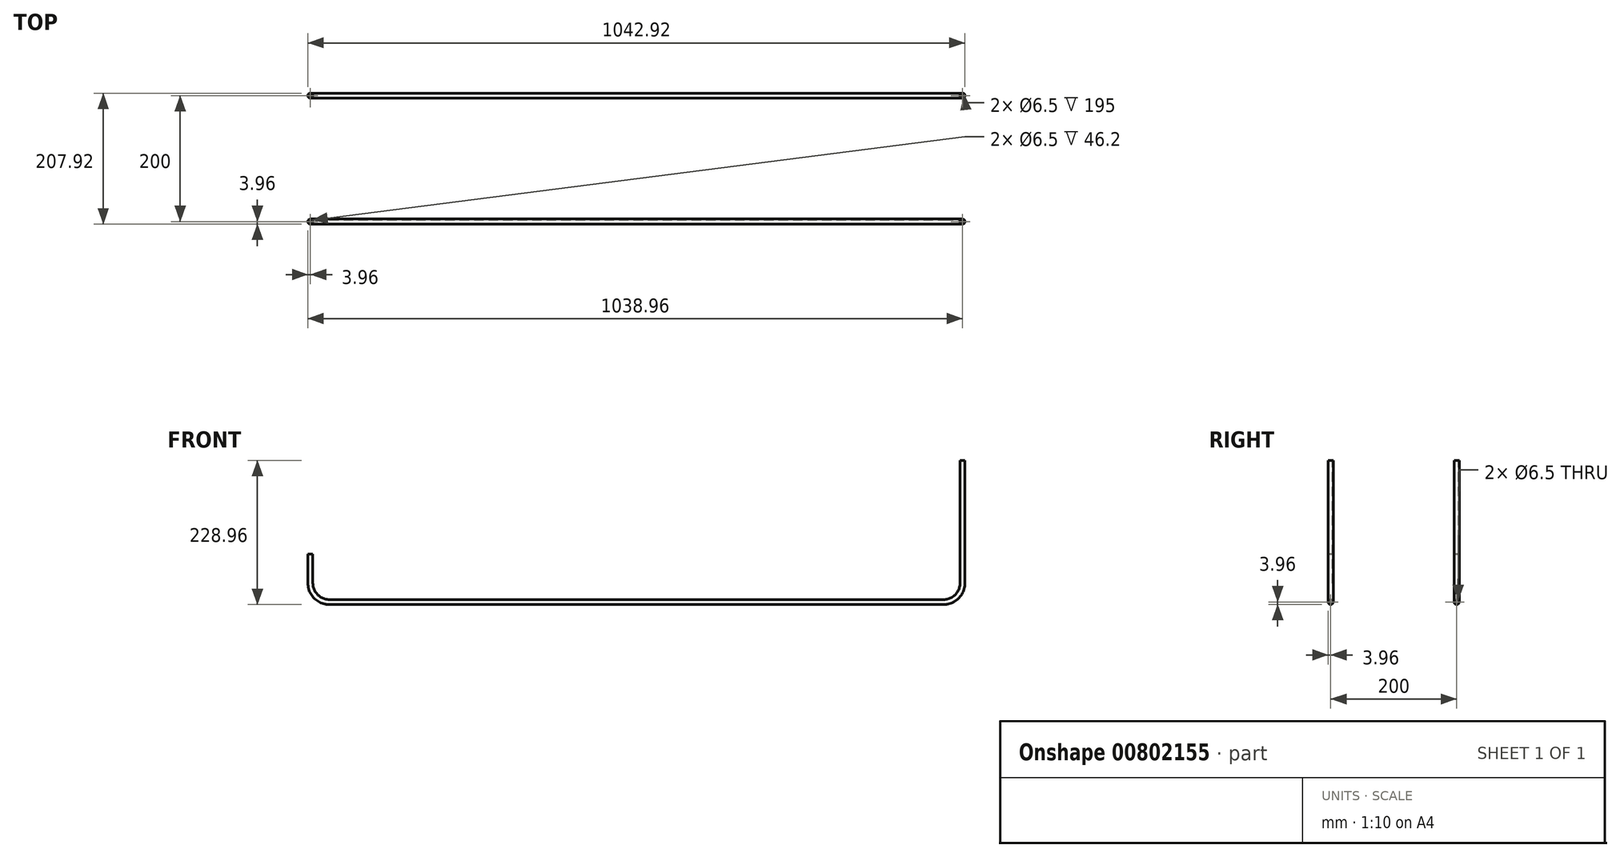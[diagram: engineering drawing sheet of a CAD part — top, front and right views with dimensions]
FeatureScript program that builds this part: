
annotation { "Feature Type Name" : "Feature", "Feature Type Description" : "" }
export const myFeature = defineFeature(function(context is Context, id is Id, definition is map)
    precondition{}
    {
        {
            var Q0;
            Q0=qCreatedBy(makeId("Right.planeOp"),FACE);
            var sketch = newSketch(context, id + "F0", { "sketchPlane" : qUnion([Q0])});
            skCircle(sketch, "E0", {"center": v(0, 0) * mm, "radius": 4.76 * mm});
            skCircle(sketch, "E1", {"center": v(0, 0) * mm, "radius": 4 * mm});
            skSolve(sketch);
        }
        {
            var Q0;
            Q0=qSketchRegion(id+"F0",true);
            extrude(context, id + "F1", {"entities" : qUnion([Q0]), "depth" : 35 * mm});
        }
        {
            var Q0;
            Q0=qSketchRegion(id+"F0",true);
            extrude(context, id + "F2", {"entities" : qUnion([Q0]), "oppositeDirection" : true, "depth" : 66.5 * mm, "offsetDistance" : 25 * mm});
        }
        {
            var Q0;
            Q0=qSketchRegion(id+"F0",true);
            extrude(context, id + "F3", {"entities" : qUnion([Q0]), "depth" : 1035 * mm, "offsetDistance" : 25 * mm});
        }
        {
            var Q0;
            Q0=makeQuery(id+"F2.opExtrude","SWEPT_BODY",BODY,{"disambiguationData":[OSD([sQuery(id+"F0.wireOp",EDGE,"E0"),sQuery(id+"F0.wireOp",EDGE,"E1")])]});
            var Q1;
            Q1=makeQuery(id+"F1.opExtrude","SWEPT_BODY",BODY,{"disambiguationData":[OSD([sQuery(id+"F0.wireOp",EDGE,"E0"),sQuery(id+"F0.wireOp",EDGE,"E1")])]});
            deleteBodies(context, id + "F4", {"entities" : qUnion([Q0, Q1])});
        }
        {
            var Q0;
            Q0=qSketchRegion(id+"F0",true);
            extrude(context, id + "F5", {"entities" : qUnion([Q0]), "oppositeDirection" : true, "depth" : 1035 * mm, "offsetDistance" : 25 * mm});
        }
        {
            var Q0;
            Q0=qCreatedBy(makeId("Front.planeOp"),FACE);
            var sketch = newSketch(context, id + "F6", { "sketchPlane" : qUnion([Q0])});
            skLineSegment(sketch, "E2", {"start": v(30, 0) * mm, "end": v(1005, 0) * mm});
            skLineSegment(sketch, "E3", {"start": v(1035, 30) * mm, "end": v(1035, 225) * mm});
            skLineSegment(sketch, "E4", {"start": v(0, 30) * mm, "end": v(0, 76.2) * mm});
            skPoint(sketch, "E5.visualSharp", {"position": v(0, 0) * mm});
            skArc(sketch, "E5.filletArc", {"start": v(0, 30) * mm, "mid": v(8.79, 8.79) * mm, "end": v(30, 0) * mm});
            skPoint(sketch, "E6.visualSharp", {"position": v(1035, 0) * mm});
            skArc(sketch, "E6.filletArc", {"start": v(1005, 0) * mm, "mid": v(1026.21, 8.79) * mm, "end": v(1035, 30) * mm});
            skPoint(sketch, "E7", {"position": v(0, 76.2) * mm});
            skSolve(sketch);
        }
        {
            var Q0;
            Q0=qCreatedBy(makeId("Top.planeOp"),FACE);
            cPlane(context, id + "F7", {"entities" : qUnion([Q0]), "cplaneType" : CPlaneType.OFFSET, "offset" : 76.2 * mm, "width" : 150 * mm, "height" : 150 * mm});
        }
        {
            var Q0;
            Q0=qCreatedBy(id+"F7.planeOp",FACE);
            var sketch = newSketch(context, id + "F8", { "sketchPlane" : qUnion([Q0])});
            skCircle(sketch, "E8", {"center": v(0, 0) * mm, "radius": 3.25 * mm});
            skCircle(sketch, "E9", {"center": v(0, 0) * mm, "radius": 3.96 * mm});
            skSolve(sketch);
        }
        {
            var Q0;
            Q0=qSketchRegion(id+"F8",true);
            var Q1;
            Q1=qConstructionFilter(qBodyType(qCreatedBy(id+"F6",EDGE),BodyType.WIRE),ConstructionObject.NO);
            sweep(context, id + "F9", {"profiles" : qUnion([Q0]), "path" : qUnion([Q1])});
        }
        {
            var Q0;
            Q0=qCreatedBy(makeId("Front.planeOp"),FACE);
            cPlane(context, id + "F10", {"entities" : qUnion([Q0]), "cplaneType" : CPlaneType.OFFSET, "offset" : 100 * mm, "width" : 150 * mm, "height" : 150 * mm});
        }
        {
            var Q0;
            Q0=makeQuery(id+"F9.opSweep","SWEPT_BODY",BODY,{"disambiguationData":[OSD([sQuery(id+"F6.wireOp",EDGE,"E3"),sQuery(id+"F8.wireOp",EDGE,"E8"),sQuery(id+"F8.wireOp",EDGE,"E9")])]});
            var Q1;
            Q1=qCreatedBy(id+"F10.planeOp",FACE);
            mirror(context, id + "F11", {"entities" : qUnion([Q0]), "mirrorPlane" : qUnion([Q1])});
        }
        {
            var Q0;
            Q0=makeQuery(id+"F5.opExtrude","SWEPT_BODY",BODY,{"disambiguationData":[OSD([sQuery(id+"F0.wireOp",EDGE,"E0"),sQuery(id+"F0.wireOp",EDGE,"E1")])]});
            var Q1;
            Q1=makeQuery(id+"F3.opExtrude","SWEPT_BODY",BODY,{"disambiguationData":[OSD([sQuery(id+"F0.wireOp",EDGE,"E0"),sQuery(id+"F0.wireOp",EDGE,"E1")])]});
            deleteBodies(context, id + "F12", {"entities" : qUnion([Q0, Q1])});
        }
    });
